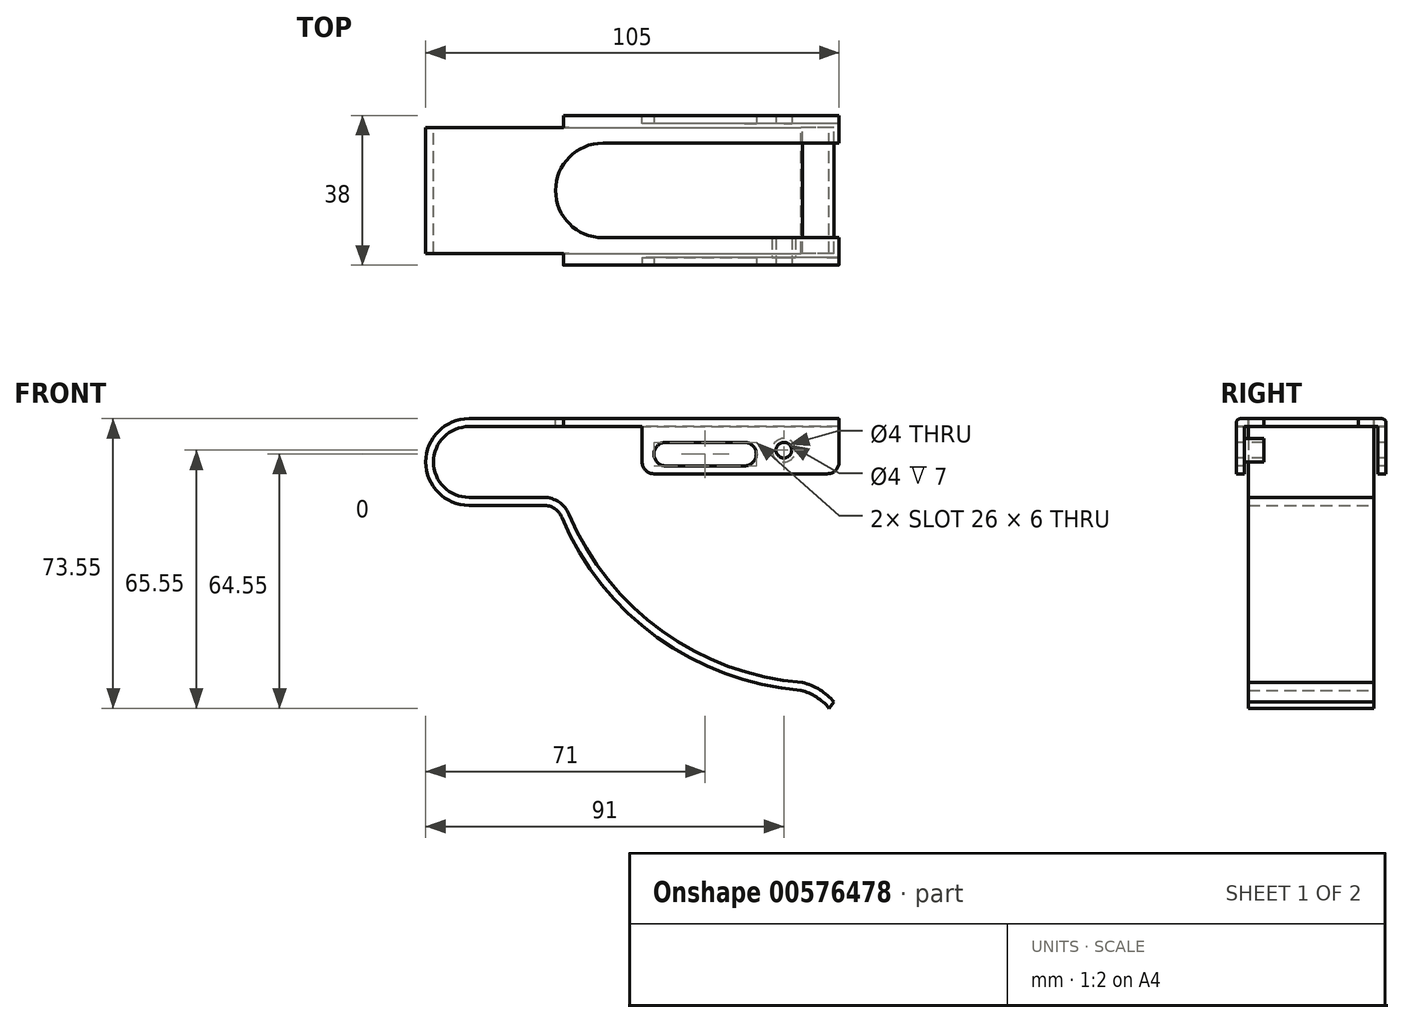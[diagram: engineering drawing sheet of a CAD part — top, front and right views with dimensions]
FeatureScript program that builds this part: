
annotation { "Feature Type Name" : "Feature", "Feature Type Description" : "" }
export const myFeature = defineFeature(function(context is Context, id is Id, definition is map)
    precondition{}
    {
        {
            var Q0;
            Q0=qCreatedBy(makeId("Front.planeOp"),FACE);
            var sketch = newSketch(context, id + "F0", { "sketchPlane" : qUnion([Q0])});
            skArc(sketch, "E0", {"start": v(0, 11) * mm, "mid": v(-11, 0) * mm, "end": v(0, -11) * mm});
            skLineSegment(sketch, "E1", {"start": v(0, 11) * mm, "end": v(94, 11) * mm});
            skLineSegment(sketch, "E2", {"start": v(0, -11) * mm, "end": v(19, -11) * mm});
            skArc(sketch, "E3", {"start": v(23.61, -14.06) * mm, "mid": v(47.82, -44.55) * mm, "end": v(84.37, -57.98) * mm});
            skArc(sketch, "E4", {"start": v(91.49, -62.55) * mm, "mid": v(88.28, -59.72) * mm, "end": v(84.37, -57.98) * mm});
            skPoint(sketch, "E5.visualSharp", {"position": v(22.4, -11) * mm});
            skArc(sketch, "E5.filletArc", {"start": v(23.61, -14.06) * mm, "mid": v(21.77, -11.84) * mm, "end": v(19, -11) * mm});
            skLineSegment(sketch, "E6.0", {"start": v(0, 9) * mm, "end": v(94, 9) * mm});
            skArc(sketch, "E6.1", {"start": v(0, 9) * mm, "mid": v(-9, 0) * mm, "end": v(0, -9) * mm});
            skArc(sketch, "E6.2", {"start": v(92.8, -61) * mm, "mid": v(89.13, -57.89) * mm, "end": v(84.7, -56) * mm});
            skArc(sketch, "E6.3", {"start": v(25.45, -13.3) * mm, "mid": v(49.07, -42.99) * mm, "end": v(84.7, -56) * mm});
            skArc(sketch, "E6.4", {"start": v(25.45, -13.3) * mm, "mid": v(22.88, -10.17) * mm, "end": v(19, -9) * mm});
            skLineSegment(sketch, "E6.5", {"start": v(0, -9) * mm, "end": v(19, -9) * mm});
            skLineSegment(sketch, "E7", {"start": v(94, 11) * mm, "end": v(94, 9) * mm});
            skLineSegment(sketch, "E8", {"start": v(92.8, -61) * mm, "end": v(91.49, -62.55) * mm});
            skLineSegment(sketch, "E9", {"start": v(92.8, -61) * mm, "end": v(104.54, -61) * mm, "construction": true});
            skSolve(sketch);
        }
        {
            var Q0;
            Q0 = qSketchRegion(id + "F0", true);
            extrude(context, id + "F1", {"entities" : qUnion([Q0]), "depth" : 16 * mm, "offsetDistance" : 25 * mm});
        }
        {
            var Q0;
            Q0=makeQuery(id+"F1.opExtrude","SWEPT_FACE",FACE,{"disambiguationData":[OSD([sQuery(id+"F0.wireOp",EDGE,"E1")])]});
            var sketch = newSketch(context, id + "F2", { "sketchPlane" : qUnion([Q0])});
            skLineSegment(sketch, "E10", {"start": v(94, -16) * mm, "end": v(94, -19) * mm});
            skLineSegment(sketch, "E11", {"start": v(94, -19) * mm, "end": v(24, -19) * mm});
            skLineSegment(sketch, "E12", {"start": v(24, -19) * mm, "end": v(24, -16) * mm});
            skSolve(sketch);
        }
        {
            var Q0;
            {var subQ0=sQuery(id+"F2.wireOp",EDGE,"E10");Q0=makeQuery(id+"F2.imprint","IMPRINT",FACE,{"disambiguationData":[TD([[makeQuery(id+"F2.imprint","IMPRINT",EDGE,{"derivedFrom":subQ0}),-1.0]])]});}
            extrude(context, id + "F3", {"entities" : qUnion([Q0]), "operationType" : NewBodyOperationType.ADD, "oppositeDirection" : true, "depth" : 2 * mm, "offsetDistance" : 25 * mm});
        }
        {
            var Q0;
            Q0=makeQuery(id+"F3.opExtrude","SWEPT_FACE",FACE,{"disambiguationData":[OSD([sQuery(id+"F2.wireOp",EDGE,"E11")])]});
            var sketch = newSketch(context, id + "F4", { "sketchPlane" : qUnion([Q0])});
            skLineSegment(sketch, "E13", {"start": v(94, 11) * mm, "end": v(94, -3) * mm});
            skLineSegment(sketch, "E14", {"start": v(94, -3) * mm, "end": v(44, -3) * mm});
            skLineSegment(sketch, "E15", {"start": v(44, -3) * mm, "end": v(44, 11) * mm});
            skSolve(sketch);
        }
        {
            var Q0;
            {var subQ3=sQuery(id+"F4.wireOp",EDGE,"E14");Q0=makeQuery(id+"F4.imprint","IMPRINT",FACE,{"disambiguationData":[TD([[makeQuery(id+"F4.imprint","IMPRINT",EDGE,{"derivedFrom":subQ3}),-1.0]])]});}
            extrude(context, id + "F5", {"entities" : qUnion([Q0]), "operationType" : NewBodyOperationType.ADD, "oppositeDirection" : true, "depth" : 2 * mm, "offsetDistance" : 25 * mm});
        }
        {
            var Q0;
            Q0=makeQuery(id+"F3.opExtrude","CAP_EDGE",EDGE,{"disambiguationData":[OSD([sQuery(id+"F2.wireOp",EDGE,"E11")])],"isStart":true});
            fillet(context, id + "F6", {"entities" : qUnion([Q0]), "radius" : 1 * mm, "allowEdgeOverflow" : false});
        }
        {
            var Q0;
            Q0=makeQuery(id+"F1.opExtrude","SWEPT_BODY",BODY,{"disambiguationData":[OSD([sQuery(id+"F0.wireOp",EDGE,"E0"),sQuery(id+"F0.wireOp",EDGE,"E1"),sQuery(id+"F0.wireOp",EDGE,"E2"),sQuery(id+"F0.wireOp",EDGE,"E3"),sQuery(id+"F0.wireOp",EDGE,"E4"),sQuery(id+"F0.wireOp",EDGE,"E5.filletArc"),sQuery(id+"F0.wireOp",EDGE,"E6.0"),sQuery(id+"F0.wireOp",EDGE,"E6.1"),sQuery(id+"F0.wireOp",EDGE,"E6.2"),sQuery(id+"F0.wireOp",EDGE,"E6.3"),sQuery(id+"F0.wireOp",EDGE,"E6.4"),sQuery(id+"F0.wireOp",EDGE,"E6.5"),sQuery(id+"F0.wireOp",EDGE,"E7"),sQuery(id+"F0.wireOp",EDGE,"E8")])]});
            var Q1;
            Q1=qCreatedBy(makeId("Front.planeOp"),FACE);
            mirror(context, id + "F7", {"operationType" : NewBodyOperationType.ADD, "entities" : qUnion([Q0]), "mirrorPlane" : qUnion([Q1])});
        }
        {
            var Q0;
            {var subQ0=sQuery(id+"F0.wireOp",EDGE,"E1");var subQ1=makeQuery(id+"F3.boolean.opBoolean","MERGE",FACE,{"derivedFrom":[makeQuery(id+"F1.opExtrude","SWEPT_FACE",FACE,{"disambiguationData":[OSD([subQ0])]}),makeQuery(id+"F3.opExtrude","CAP_FACE",FACE,{"disambiguationData":[OSD([subQ0,sQuery(id+"F2.wireOp",EDGE,"E10"),sQuery(id+"F2.wireOp",EDGE,"E11"),sQuery(id+"F2.wireOp",EDGE,"E12")])],"isStart":true})]});Q0=makeQuery(id+"F7.boolean.opBoolean","MERGE",FACE,{"derivedFrom":[subQ1,makeQuery(id+"F7.opPattern","COPY",FACE,{"derivedFrom":subQ1,"instanceName":"1"})]});}
            var sketch = newSketch(context, id + "F8", { "sketchPlane" : qUnion([Q0])});
            skArc(sketch, "E16", {"start": v(34, 12) * mm, "mid": v(22, 0) * mm, "end": v(34, -12) * mm});
            skLineSegment(sketch, "E17", {"start": v(34, 12) * mm, "end": v(94, 12) * mm});
            skLineSegment(sketch, "E18", {"start": v(34, -12) * mm, "end": v(94, -12) * mm});
            skLineSegment(sketch, "E19", {"start": v(94, 12) * mm, "end": v(94, -12) * mm});
            skSolve(sketch);
        }
        {
            var Q0;
            Q0 = qSketchRegion(id + "F8", true);
            extrude(context, id + "F9", {"entities" : qUnion([Q0]), "operationType" : NewBodyOperationType.REMOVE, "oppositeDirection" : true, "depth" : 2 * mm, "offsetDistance" : 25 * mm});
        }
        {
            var Q0;
            {var subQ0=sQuery(id+"F2.wireOp",EDGE,"E11");Q0=makeQuery(id+"F5.boolean.opBoolean","MERGE",FACE,{"derivedFrom":[makeQuery(id+"F3.opExtrude","SWEPT_FACE",FACE,{"disambiguationData":[OSD([subQ0])]}),makeQuery(id+"F5.opExtrude","CAP_FACE",FACE,{"disambiguationData":[OSD([subQ0,sQuery(id+"F4.wireOp",EDGE,"E13"),sQuery(id+"F4.wireOp",EDGE,"E14"),sQuery(id+"F4.wireOp",EDGE,"E15")])],"isStart":true})]});}
            var sketch = newSketch(context, id + "F10", { "sketchPlane" : qUnion([Q0])});
            skLineSegment(sketch, "E20", {"start": v(50, 2) * mm, "end": v(70, 2) * mm});
            skArc(sketch, "E21.0.startCap", {"start": v(50, -1) * mm, "mid": v(47, 2) * mm, "end": v(50, 5) * mm});
            skArc(sketch, "E21.0.endCap", {"start": v(70, 5) * mm, "mid": v(73, 2) * mm, "end": v(70, -1) * mm});
            skLineSegment(sketch, "E21.0.left", {"start": v(50, 5) * mm, "end": v(70, 5) * mm});
            skLineSegment(sketch, "E21.0.right", {"start": v(50, -1) * mm, "end": v(70, -1) * mm});
            skSolve(sketch);
        }
        {
            var Q0;
            Q0 = qSketchRegion(id + "F10", true);
            extrude(context, id + "F11", {"entities" : qUnion([Q0]), "operationType" : NewBodyOperationType.REMOVE, "endBound" : BoundingType.THROUGH_ALL, "oppositeDirection" : true, "depth" : 25 * mm, "offsetDistance" : 25 * mm});
        }
        {
            var Q0;
            {var subQ0=sQuery(id+"F2.wireOp",EDGE,"E11");Q0=makeQuery(id+"F5.boolean.opBoolean","MERGE",FACE,{"derivedFrom":[makeQuery(id+"F3.opExtrude","SWEPT_FACE",FACE,{"disambiguationData":[OSD([subQ0])]}),makeQuery(id+"F5.opExtrude","CAP_FACE",FACE,{"disambiguationData":[OSD([subQ0,sQuery(id+"F4.wireOp",EDGE,"E13"),sQuery(id+"F4.wireOp",EDGE,"E14"),sQuery(id+"F4.wireOp",EDGE,"E15")])],"isStart":true})]});}
            var sketch = newSketch(context, id + "F12", { "sketchPlane" : qUnion([Q0])});
            skPoint(sketch, "E22", {"position": v(80, 3) * mm});
            skSolve(sketch);
        }
        {
            var Q0;
            Q0=sQuery(id+"F12.wireOp",VERTEX,"E22");
            var Q1;
            Q1=makeQuery(id+"F1.opExtrude","SWEPT_BODY",BODY,{"disambiguationData":[OSD([sQuery(id+"F0.wireOp",EDGE,"E0"),sQuery(id+"F0.wireOp",EDGE,"E1"),sQuery(id+"F0.wireOp",EDGE,"E2"),sQuery(id+"F0.wireOp",EDGE,"E3"),sQuery(id+"F0.wireOp",EDGE,"E4"),sQuery(id+"F0.wireOp",EDGE,"E5.filletArc"),sQuery(id+"F0.wireOp",EDGE,"E6.0"),sQuery(id+"F0.wireOp",EDGE,"E6.1"),sQuery(id+"F0.wireOp",EDGE,"E6.2"),sQuery(id+"F0.wireOp",EDGE,"E6.3"),sQuery(id+"F0.wireOp",EDGE,"E6.4"),sQuery(id+"F0.wireOp",EDGE,"E6.5"),sQuery(id+"F0.wireOp",EDGE,"E7"),sQuery(id+"F0.wireOp",EDGE,"E8")])]});
            hole(context, id + "F13", {"style" : HoleStyle.SIMPLE, "endStyle" : HoleEndStyle.THROUGH, "holeDiameter" : 4 * mm, "majorDiameter" : 5 * mm, "isTappedThrough" : true, "tappedDepth" : 12 * mm, "tapClearance" : 3, "locations" : qUnion([Q0]), "scope" : qUnion([Q1])});
        }
        {
            var Q0;
            Q0=makeQuery(id+"F5.opExtrude","CAP_FACE",FACE,{"disambiguationData":[OSD([sQuery(id+"F2.wireOp",EDGE,"E11"),sQuery(id+"F4.wireOp",EDGE,"E13"),sQuery(id+"F4.wireOp",EDGE,"E14"),sQuery(id+"F4.wireOp",EDGE,"E15")])],"isStart":false});
            var sketch = newSketch(context, id + "F14", { "sketchPlane" : qUnion([Q0])});
            skCircle(sketch, "E23.0", {"center": v(-80, 3) * mm, "radius": 2 * mm});
            skCircle(sketch, "E24.0", {"center": v(-80, 3) * mm, "radius": 3 * mm});
            skSolve(sketch);
        }
        {
            var Q0;
            Q0 = qSketchRegion(id + "F14", true);
            extrude(context, id + "F15", {"entities" : qUnion([Q0]), "operationType" : NewBodyOperationType.ADD, "depth" : 5 * mm, "offsetDistance" : 25 * mm});
        }
        {
            var Q0;
            Q0=makeQuery(id+"F7.opPattern","COPY",EDGE,{"derivedFrom":makeQuery(id+"F5.opExtrude","SWEPT_EDGE",EDGE,{"disambiguationData":[OSD([sQuery(id+"F4.wireOp",EDGE,"E13"),sQuery(id+"F4.wireOp",EDGE,"E14")])]}),"instanceName":"1"});
            var Q1;
            Q1=makeQuery(id+"F7.opPattern","COPY",EDGE,{"derivedFrom":makeQuery(id+"F5.opExtrude","SWEPT_EDGE",EDGE,{"disambiguationData":[OSD([sQuery(id+"F4.wireOp",EDGE,"E14"),sQuery(id+"F4.wireOp",EDGE,"E15")])]}),"instanceName":"1"});
            var Q2;
            Q2=makeQuery(id+"F5.opExtrude","SWEPT_EDGE",EDGE,{"disambiguationData":[OSD([sQuery(id+"F4.wireOp",EDGE,"E13"),sQuery(id+"F4.wireOp",EDGE,"E14")])]});
            var Q3;
            Q3=makeQuery(id+"F5.opExtrude","SWEPT_EDGE",EDGE,{"disambiguationData":[OSD([sQuery(id+"F4.wireOp",EDGE,"E14"),sQuery(id+"F4.wireOp",EDGE,"E15")])]});
            fillet(context, id + "F16", {"entities" : qUnion([Q0, Q1, Q2, Q3]), "radius" : 3 * mm, "tangentPropagation" : true, "allowEdgeOverflow" : false});
        }
    });
